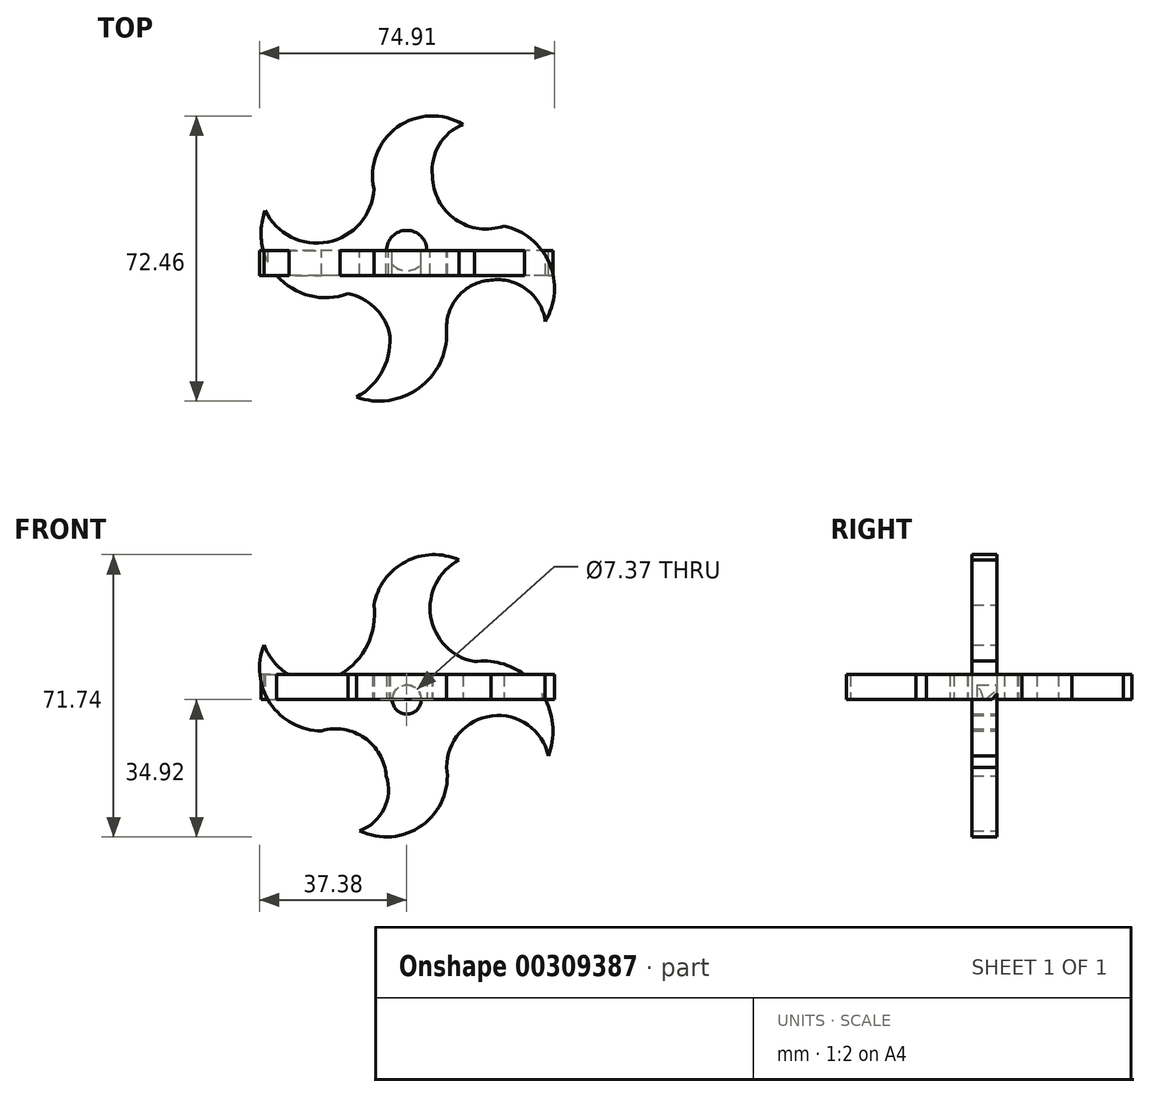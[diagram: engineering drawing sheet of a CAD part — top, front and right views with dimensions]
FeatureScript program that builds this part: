
annotation { "Feature Type Name" : "Feature", "Feature Type Description" : "" }
export const myFeature = defineFeature(function(context is Context, id is Id, definition is map)
    precondition{}
    {
        {
            var Q0;
            Q0=qCreatedBy(makeId("Front.planeOp"),FACE);
            var sketch = newSketch(context, id + "F0", { "sketchPlane" : qUnion([Q0])});
            skCircle(sketch, "E0", {"center": v(0, 0) * mm, "radius": 3.69 * mm});
            skArc(sketch, "E1", {"start": v(13.3, 35.44) * mm, "mid": v(-0.33, 35.01) * mm, "end": v(-8.34, 23.98) * mm});
            skArc(sketch, "E2", {"start": v(13.3, 35.44) * mm, "mid": v(6.1, 21.16) * mm, "end": v(17.2, 9.64) * mm});
            skArc(sketch, "E3", {"start": v(35.97, -14.33) * mm, "mid": v(33.39, 2.98) * mm, "end": v(17.2, 9.64) * mm});
            skArc(sketch, "E4", {"start": v(35.97, -14.33) * mm, "mid": v(30.78, -6.45) * mm, "end": v(21.63, -4.17) * mm});
            skArc(sketch, "E5", {"start": v(21.63, -4.17) * mm, "mid": v(13.42, -8.5) * mm, "end": v(10.16, -17.2) * mm});
            skArc(sketch, "E6", {"start": v(-11.99, -33.36) * mm, "mid": v(3.95, -31.94) * mm, "end": v(10.16, -17.2) * mm});
            skArc(sketch, "E7", {"start": v(-11.99, -33.36) * mm, "mid": v(-5.76, -27.76) * mm, "end": v(-5.2, -19.4) * mm});
            skArc(sketch, "E8", {"start": v(-5.2, -19.4) * mm, "mid": v(-10.69, -9.76) * mm, "end": v(-21.63, -7.95) * mm});
            skArc(sketch, "E9", {"start": v(-36.23, 13.81) * mm, "mid": v(-34.7, -0.94) * mm, "end": v(-21.63, -7.95) * mm});
            skArc(sketch, "E10", {"start": v(-36.23, 13.81) * mm, "mid": v(-30.5, 6.69) * mm, "end": v(-21.63, 4.43) * mm});
            skArc(sketch, "E11", {"start": v(-21.63, 4.43) * mm, "mid": v(-11.25, 11.66) * mm, "end": v(-8.34, 23.98) * mm});
            skSolve(sketch);
        }
        {
            var Q0;
            Q0=makeQuery(id+"F0.imprint","IMPRINT",FACE,{"disambiguationData":[TD([[makeQuery(id+"F0.imprint","IMPRINT",EDGE,{"derivedFrom":sQuery(id+"F0.wireOp",EDGE,"E0")}),-1.0]])]});
            extrude(context, id + "F1", {"entities" : qUnion([Q0]), "depth" : 6.35 * mm});
        }
        {
            var Q0;
            Q0=qCreatedBy(makeId("Top.planeOp"),FACE);
            var sketch = newSketch(context, id + "F2", { "sketchPlane" : qUnion([Q0])});
            skCircle(sketch, "E12", {"center": v(0, 0) * mm, "radius": 5.12 * mm});
            skArc(sketch, "E13", {"start": v(-35.97, 10.16) * mm, "mid": v(-32.22, -7.2) * mm, "end": v(-14.86, -10.95) * mm});
            skArc(sketch, "E14", {"start": v(-35.97, 10.16) * mm, "mid": v(-20.02, 2.16) * mm, "end": v(-8.34, 15.64) * mm});
            skArc(sketch, "E15", {"start": v(14.33, 32.06) * mm, "mid": v(-2.4, 31.3) * mm, "end": v(-8.34, 15.64) * mm});
            skArc(sketch, "E16", {"start": v(14.33, 32.06) * mm, "mid": v(8.22, 26.82) * mm, "end": v(6.54, 18.95) * mm});
            skArc(sketch, "E17", {"start": v(6.54, 18.95) * mm, "mid": v(12.38, 7.91) * mm, "end": v(24.76, 6.25) * mm});
            skArc(sketch, "E18", {"start": v(35.18, -17.98) * mm, "mid": v(36.21, -3.18) * mm, "end": v(24.76, 6.25) * mm});
            skArc(sketch, "E19", {"start": v(35.18, -17.98) * mm, "mid": v(30.48, -9.86) * mm, "end": v(21.37, -7.56) * mm});
            skArc(sketch, "E20", {"start": v(21.37, -7.56) * mm, "mid": v(13, -11.7) * mm, "end": v(10.16, -20.59) * mm});
            skArc(sketch, "E21", {"start": v(-12.77, -37.27) * mm, "mid": v(3.09, -34.97) * mm, "end": v(10.16, -20.59) * mm});
            skArc(sketch, "E22", {"start": v(-12.77, -37.27) * mm, "mid": v(-5.98, -30.24) * mm, "end": v(-4.43, -20.59) * mm});
            skArc(sketch, "E23", {"start": v(-4.43, -20.59) * mm, "mid": v(-8.31, -14.33) * mm, "end": v(-14.86, -10.95) * mm});
            skSolve(sketch);
        }
        {
            var Q0;
            Q0=makeQuery(id+"F2.imprint","IMPRINT",FACE,{"disambiguationData":[TD([[makeQuery(id+"F2.imprint","IMPRINT",EDGE,{"derivedFrom":sQuery(id+"F2.wireOp",EDGE,"E12")}),-1.0]])]});
            extrude(context, id + "F3", {"entities" : qUnion([Q0]), "operationType" : NewBodyOperationType.ADD, "depth" : 6.35 * mm});
        }
    });
